# Revit family: Power-ModularDevices-GEWISS-90AM-SWITCH_ON_OFF
name_source: partatom
category: Apparecchi elettrici
revit_build: Autodesk Revit 2016 (Build: 20161004_0715(x64)
units: mm (PartAtom-declared; Revit-internal decimal feet)

## family parameters
Condiviso = No
Host = Superficie
Mantenere orientamento annotazione = Sì
Numero OmniClass = 23.80.30.14
Punto di calcolo locali = Sì
Quota connettore circolare = Usa diametro
Taglio con vuoti quando caricato = No
Tipo di parte = Normale
Titolo OmniClass = Power Distribution

## types (4) — shared parameters
A = 54 mm  [stored 0.177165 ft]
B = 85 mm  [stored 0.278871 ft]
C = 65 mm  [stored 0.213255 ft]
Catalogue = POWER
Catalogue Range = 90 AM
Characteristics = With red indicator lamp
D = 45 mm  [stored 0.147638 ft]
Electrocod = 1421
Fin_nterruttore = <Per categoria>
IDF = ca8755d7-c1ca-4274-ad7b-33f739b1c151
IDT = f30bf467-093b-4f72-8385-68cf8ffc79e1
Immagine tipo = GW96542.jpg
No. Chorus modules = 1
Numero poli = 1
Potenza in Watt = 0 V
Produttore = GEWISS S.p.A.
Prospetto di default = 1219 mm
Rated voltage = 230V
TEXT LABEL = A
Technical sheet = https://www.gewiss.com
Type = With indicator lamp
URL = https://www.gewiss.com
Version file RFA = 18.0

## per-type parameters (varying)
| type | Descrizione | EAN code | Modello | Number of poles | Rated current (In) |
| GW96539 - ON-OFF SWITCH+IND.LAMP 16A 1P 230V 1M | ON-OFF SWITCH+IND.LAMP 16A 1P 230V 1M | 8011564447745 | GW96539 | 1P | 16A |
| GW96541 - ON-OFF SWITCH+IND.LAMP 16A 2P 230V 1M | ON-OFF SWITCH+IND.LAMP 16A 2P 230V 1M | 8011564447905 | GW96541 | 2P | 16A |
| GW96540 - ON-OFF SWITCH+IND.LAMP 32A 1P 230V 1M | ON-OFF SWITCH+IND.LAMP 32A 1P 230V 1M | 8011564447899 | GW96540 | 1P | 32A |
| GW96542 - ON-OFF SWITCH+IND.LAMP 32A 2P 230V 1M | ON-OFF SWITCH+IND.LAMP 32A 2P 230V 1M | 8011564447912 | GW96542 | 2P | 32A |

note: [stored X ft] marks values corroborated as IEEE doubles in the binary element streams (Revit-internal decimal feet)
